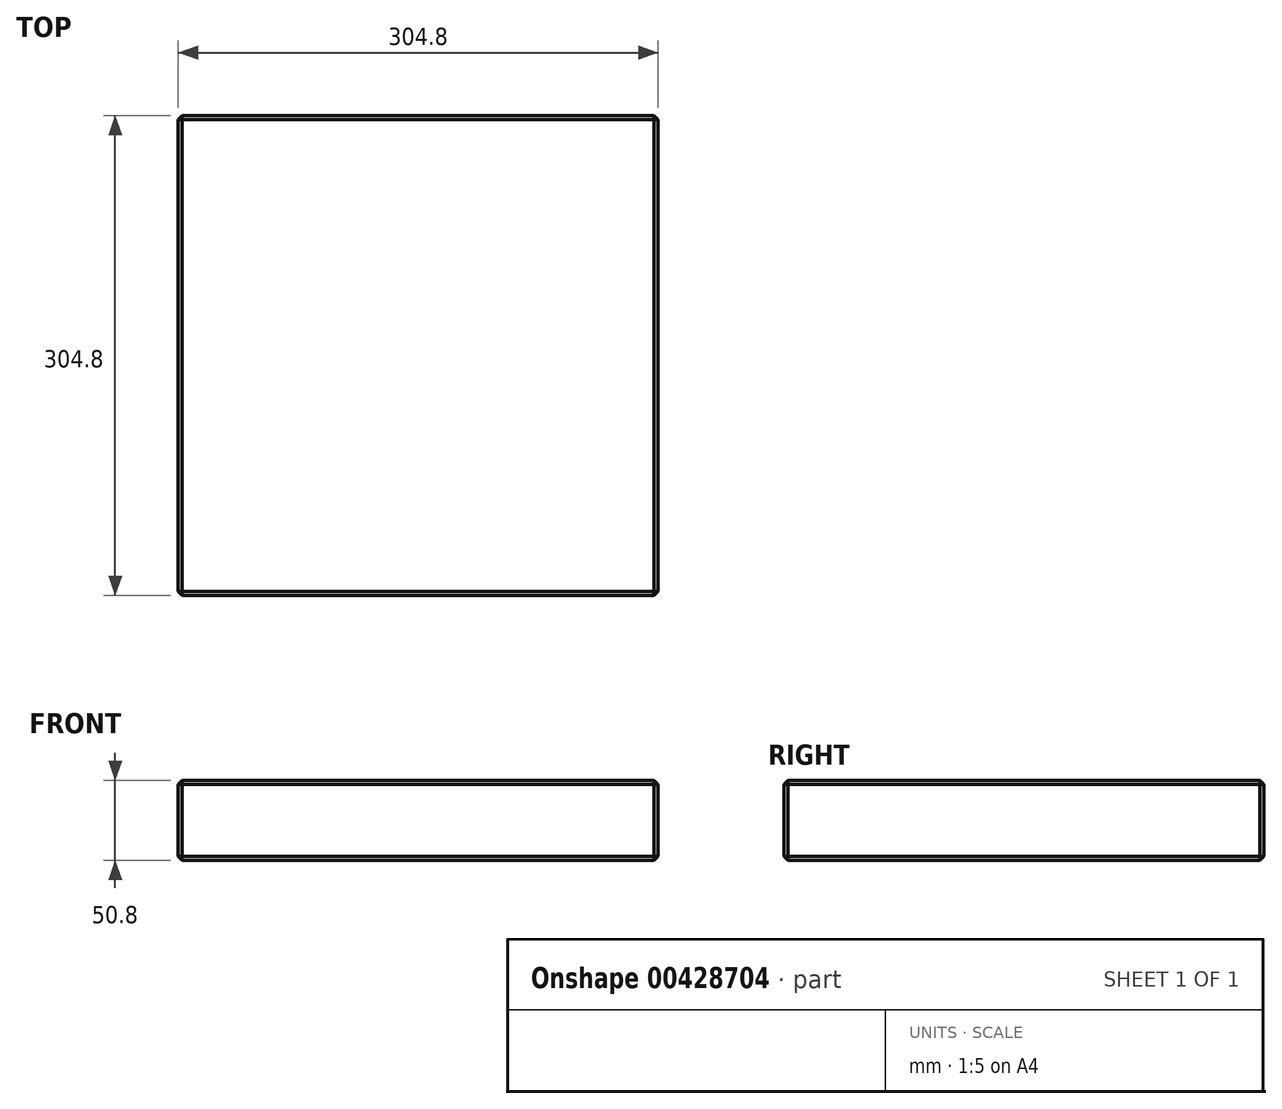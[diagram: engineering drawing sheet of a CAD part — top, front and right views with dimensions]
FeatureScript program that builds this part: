
annotation { "Feature Type Name" : "Feature", "Feature Type Description" : "" }
export const myFeature = defineFeature(function(context is Context, id is Id, definition is map)
    precondition{}
    {
        {
            var Q0;
            Q0=qCreatedBy(makeId("Top.planeOp"),FACE);
            var sketch = newSketch(context, id + "F0", { "sketchPlane" : qUnion([Q0])});
            skLineSegment(sketch, "E0.bottom", {"start": v(0, 0) * mm, "end": v(304.8, 0) * mm});
            skLineSegment(sketch, "E0.top", {"start": v(0, 304.8) * mm, "end": v(304.8, 304.8) * mm});
            skLineSegment(sketch, "E0.left", {"start": v(0, 0) * mm, "end": v(0, 304.8) * mm});
            skLineSegment(sketch, "E0.right", {"start": v(304.8, 0) * mm, "end": v(304.8, 304.8) * mm});
            skSolve(sketch);
        }
        {
            var Q0;
            Q0=makeQuery(id+"F0.imprint","IMPRINT",FACE,{"disambiguationData":[TD([[makeQuery(id+"F0.imprint","IMPRINT",EDGE,{"derivedFrom":sQuery(id+"F0.wireOp",EDGE,"E0.bottom")}),1.0]])]});
            extrude(context, id + "F1", {"entities" : qUnion([Q0]), "depth" : 50.8 * mm, "offsetDistance" : 25.4 * mm});
        }
        {
            var Q0;
            Q0=makeQuery(id+"F1.opExtrude","CAP_EDGE",EDGE,{"disambiguationData":[OSD([sQuery(id+"F0.wireOp",EDGE,"E0.left")])],"isStart":false});
            var Q1;
            Q1=makeQuery(id+"F1.opExtrude","CAP_EDGE",EDGE,{"disambiguationData":[OSD([sQuery(id+"F0.wireOp",EDGE,"E0.bottom")])],"isStart":false});
            var Q2;
            Q2=makeQuery(id+"F1.opExtrude","SWEPT_EDGE",EDGE,{"disambiguationData":[OSD([sQuery(id+"F0.wireOp",EDGE,"E0.bottom"),sQuery(id+"F0.wireOp",EDGE,"E0.left")])]});
            var Q3;
            Q3=makeQuery(id+"F1.opExtrude","SWEPT_EDGE",EDGE,{"disambiguationData":[OSD([sQuery(id+"F0.wireOp",EDGE,"E0.bottom"),sQuery(id+"F0.wireOp",EDGE,"E0.right")])]});
            var Q4;
            Q4=makeQuery(id+"F1.opExtrude","CAP_EDGE",EDGE,{"disambiguationData":[OSD([sQuery(id+"F0.wireOp",EDGE,"E0.right")])],"isStart":false});
            var Q5;
            Q5=makeQuery(id+"F1.opExtrude","SWEPT_EDGE",EDGE,{"disambiguationData":[OSD([sQuery(id+"F0.wireOp",EDGE,"E0.top"),sQuery(id+"F0.wireOp",EDGE,"E0.right")])]});
            var Q6;
            Q6=makeQuery(id+"F1.opExtrude","CAP_EDGE",EDGE,{"disambiguationData":[OSD([sQuery(id+"F0.wireOp",EDGE,"E0.top")])],"isStart":false});
            var Q7;
            Q7=makeQuery(id+"F1.opExtrude","SWEPT_EDGE",EDGE,{"disambiguationData":[OSD([sQuery(id+"F0.wireOp",EDGE,"E0.top"),sQuery(id+"F0.wireOp",EDGE,"E0.left")])]});
            var Q8;
            Q8=makeQuery(id+"F1.opExtrude","CAP_EDGE",EDGE,{"disambiguationData":[OSD([sQuery(id+"F0.wireOp",EDGE,"E0.top")])],"isStart":true});
            var Q9;
            Q9=makeQuery(id+"F1.opExtrude","CAP_EDGE",EDGE,{"disambiguationData":[OSD([sQuery(id+"F0.wireOp",EDGE,"E0.left")])],"isStart":true});
            var Q10;
            Q10=makeQuery(id+"F1.opExtrude","CAP_EDGE",EDGE,{"disambiguationData":[OSD([sQuery(id+"F0.wireOp",EDGE,"E0.right")])],"isStart":true});
            var Q11;
            Q11=makeQuery(id+"F1.opExtrude","CAP_EDGE",EDGE,{"disambiguationData":[OSD([sQuery(id+"F0.wireOp",EDGE,"E0.bottom")])],"isStart":true});
            chamfer(context, id + "F2", {"entities" : qUnion([Q0, Q1, Q2, Q3, Q4, Q5, Q6, Q7, Q8, Q9, Q10, Q11]), "width" : 2.54 * mm, "tangentPropagation" : true});
        }
    });
